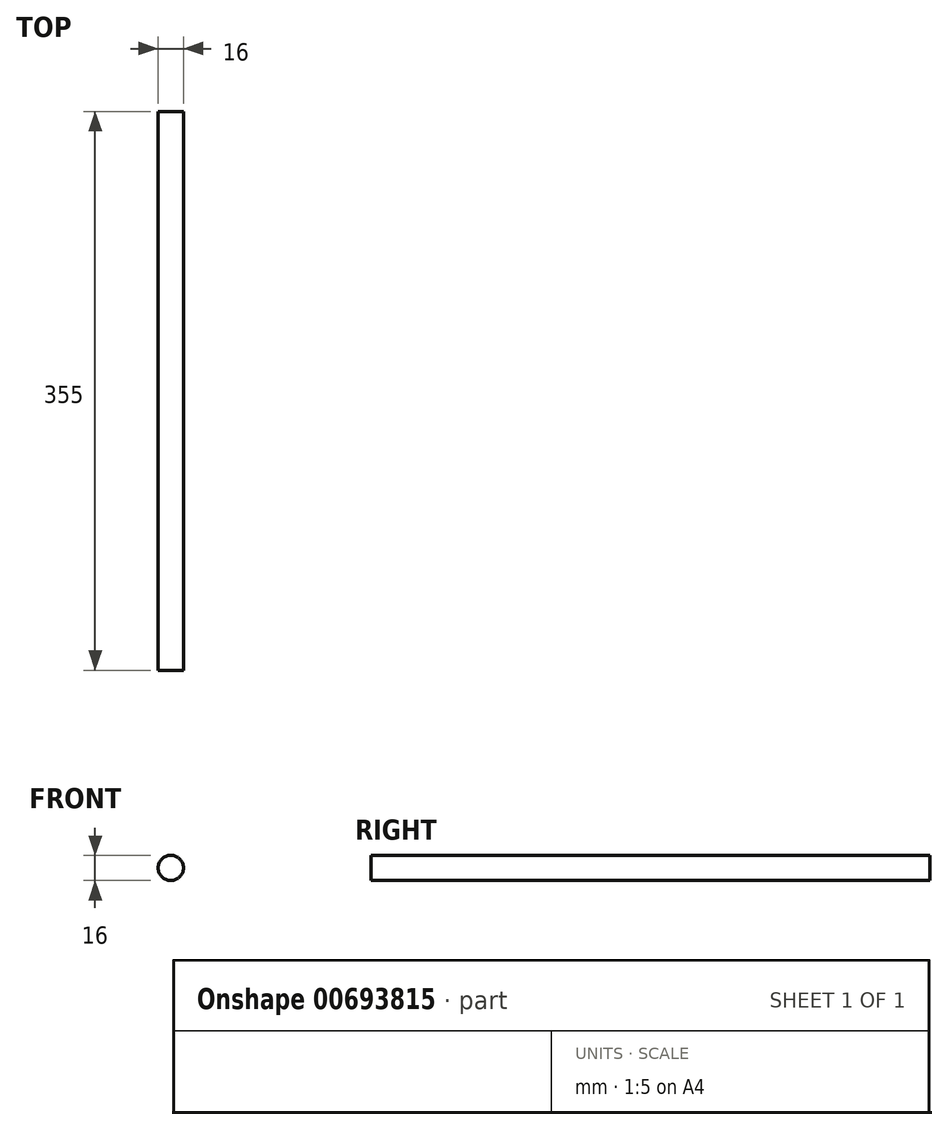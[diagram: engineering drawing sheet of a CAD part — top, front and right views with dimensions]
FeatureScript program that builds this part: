
annotation { "Feature Type Name" : "Feature", "Feature Type Description" : "" }
export const myFeature = defineFeature(function(context is Context, id is Id, definition is map)
    precondition{}
    {
        {
            var Q0;
            Q0=qCreatedBy(makeId("Front.planeOp"),FACE);
            var sketch = newSketch(context, id + "F0", { "sketchPlane" : qUnion([Q0])});
            skCircle(sketch, "E0", {"center": v(0, 0) * mm, "radius": 8 * mm});
            skSolve(sketch);
        }
        {
            var Q0;
            Q0 = qSketchRegion(id + "F0", true);
            extrude(context, id + "F1", {"entities" : qUnion([Q0]), "endBound" : BoundingType.SYMMETRIC, "depth" : 355 * mm, "offsetDistance" : 25.4 * mm});
        }
    });
